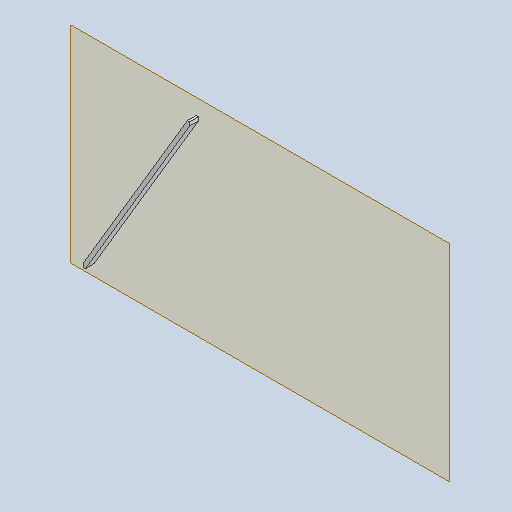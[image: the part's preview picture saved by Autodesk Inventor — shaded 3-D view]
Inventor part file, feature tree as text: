
AUTODESK INVENTOR PART (.ipt)
format: ipt  version: 2025.1 (Build 291241020, 241B)  size: 82,432 bytes
history: native  units: in
note: dims shown in document units (in); Inventor stores cm internally (conversion verified against a paired STEP export)
features: other x3, sketch x1, plane x1
ambient origin geometry x8: Origin, YZ Plane, XZ Plane, XY Plane, X Axis, Y Axis, Z Axis, Center Point
bodies: Solid1 (feature_tree)
feature tree (5):
  other  "Part11.ipt"
  other  "Solid1::Part11.ipt"
  other  "TaggingFeature1"
  sketch  "Sketch1"  dims[d0=0.3937in]
  plane  "Work Plane1"
